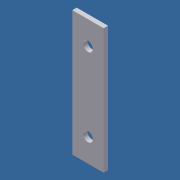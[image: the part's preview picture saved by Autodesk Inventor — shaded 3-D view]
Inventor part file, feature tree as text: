
AUTODESK INVENTOR PART (.ipt)
format: ipt  version: 2012 SP1 (Build 160190100, 190)  size: 79,360 bytes
history: native  units: in
note: dims shown in document units (in); Inventor stores cm internally (conversion verified against a paired STEP export)
features: extrude x2, sketch x2, pattern_linear x1
ambient origin geometry x8: Origin, YZ Plane, XZ Plane, XY Plane, X Axis, Y Axis, Z Axis, Center Point
bodies: Solid1 (feature_tree)
feature tree (5):
  extrude  "Extrusion1"  Depth=2.0in
  extrude  "Extrusion2"  Depth=0.1562in
  pattern_linear  "Rectangular Pattern1"  Spacing1=0.375in  [1 undecoded]
  sketch  "Sketch1"  dims[d0=0.5in d1=2.0in]
  sketch  "Sketch2"  dims[d2=0.07in d3=0.0in d4=0.1562in d5=0.375in d6=1.0in d7=0.0in d8=0.7874in d10=1.25in]
note: 1 required parameter value undecoded (feature->parameter linkage not recoverable at this tier; creation-order binding heuristic only, values carry confidence <= 0.55)
